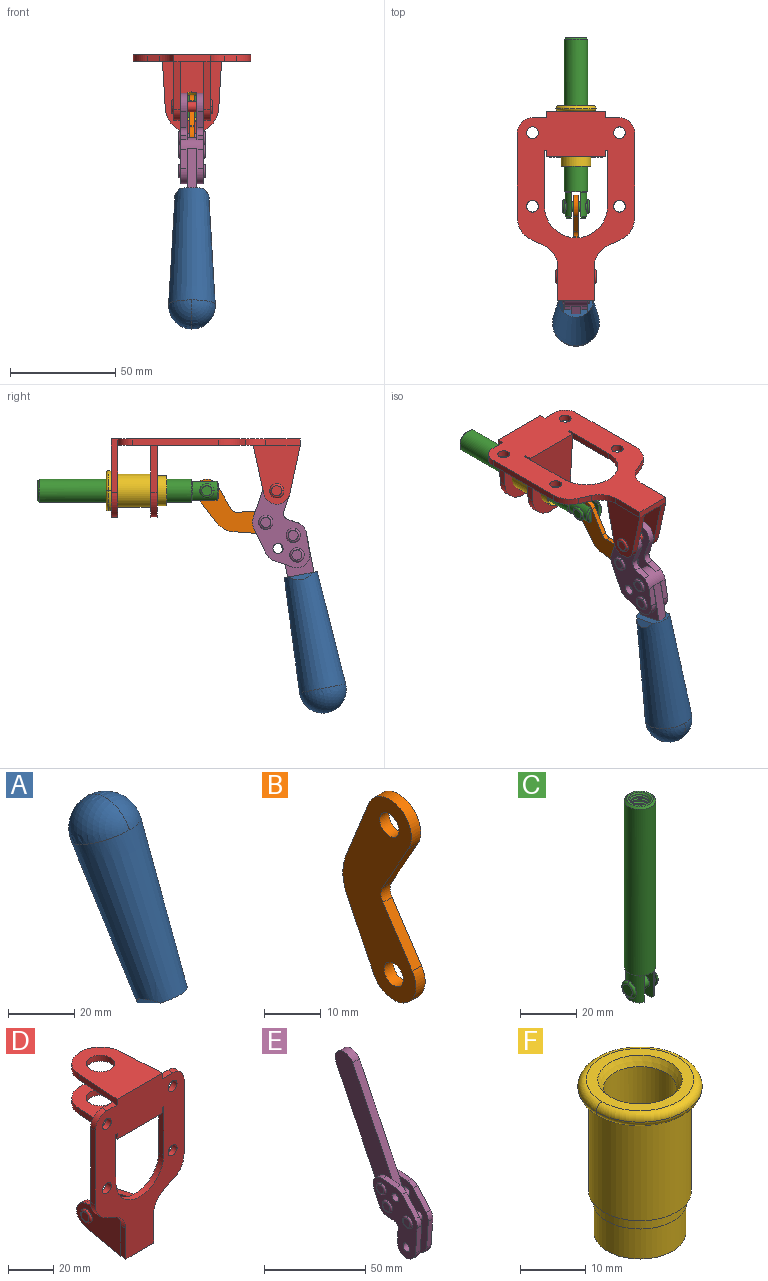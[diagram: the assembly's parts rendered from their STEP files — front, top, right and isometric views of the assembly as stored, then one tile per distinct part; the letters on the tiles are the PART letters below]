
ASSEMBLY  parts=6 mates=6
PART A: 11 faces, bbox 22.3x42.6x64.5 mm
  f0: sphere r=11.13mm, area 411.4mm2, adj f1,f8
  f1: cone r=11.11mm half-angle=3.3deg, axis (0,0.44,0.9), area 3251.8mm2, adj f0,f7,f8,f9,f10
  f2: cylinder r=6.16mm len=11.7mm, axis (1,0,0), area 89.5mm2, adj f3,f4,f5,f6
  f3: plane 60.23x36.75mm, normal (-1,0,0), area 763.6mm2, adj f2,f4,f6,f10
  f4: plane 51.37x25.05mm, normal (0,0.9,-0.44), area 264.2mm2, adj f2,f3,f5,f10
  f5: plane 60.23x36.75mm, normal (1,0,0), area 763.6mm2, adj f2,f4,f6,f10
  f6: plane 51.37x25.05mm, normal (0,-0.9,0.44), area 264.2mm2, adj f2,f3,f5,f10
  f7: plane 9.95x5.95mm, normal (0.71,-0.31,-0.64), area 25.8mm2, adj f1,f10
  f8: sphere r=11.13mm, area 411.4mm2, adj f0,f1
  f9: plane 9.95x5.95mm, normal (-0.71,-0.31,-0.64), area 25.8mm2, adj f1,f10
  f10: plane 14.27x11.38mm, normal (0,-0.44,-0.9), area 106.7mm2, adj f1,f3,f4,f5,f6,f7,f9
PART B: 12 faces, bbox 2.3x18.2x42.8 mm
  f0: cylinder r=2.4mm len=4.8mm, axis (1,0,0), area 34.9mm2, adj f4,f11
  f1: cylinder r=10.41mm len=8.47mm, axis (1,0,0), area 20.2mm2, adj f4,f9,f10,f11
  f2: cylinder r=3.05mm len=3.16mm, axis (1,0,0), area 7.7mm2, adj f4,f6,f7,f11
  f3: cylinder r=2.4mm len=4.8mm, axis (1,0,0), area 34.9mm2, adj f4,f11
  f4: plane 42.81x18.23mm, normal (-1,0,0), area 414.1mm2, adj f0,f1,f2,f3,f5,f6,f7,f8
  f5: cylinder r=5.54mm len=10.67mm, axis (1,0,0), area 41.8mm2, adj f4,f6,f10,f11
  f6: plane 11.66x6.53mm, normal (0,-0.87,-0.49), area 30.9mm2, adj f2,f4,f5,f11
  f7: plane 11.17x7.33mm, normal (0,-0.84,0.55), area 30.9mm2, adj f2,f4,f8,f11
  f8: cylinder r=5.54mm len=10.51mm, axis (1,0,0), area 41.8mm2, adj f4,f7,f9,f11
  f9: plane 13.67x6.67mm, normal (0,0.9,-0.44), area 35.1mm2, adj f1,f4,f8,f11
  f10: plane 14.1x5.7mm, normal (0,0.93,0.37), area 35.1mm2, adj f1,f4,f5,f11
  f11: plane 42.81x18.23mm, normal (1,0,0), area 414.1mm2, adj f0,f1,f2,f3,f5,f6,f7,f8
PART C: 48 faces, bbox 12.6x11.1x86.1 mm
  f0: torus R=2.41mm, axis (-1,0,0), area 15mm2, adj f30,f32,f34
  f1: torus R=2.41mm, axis (-1,0,0), area 15mm2, adj f29,f31,f33
  f2: cylinder r=5.54mm len=72.39mm, axis (0,0,1), area 2518.5mm2, adj f3,f4,f42,f43
  f3: cone r=5.54mm half-angle=45deg, axis (0,0,1), area 7.6mm2, adj f2,f5,f41
  f4: cone r=5.54mm half-angle=45deg, axis (0,0,-1), area 34.9mm2, adj f2,f39
  f5: cylinder r=5.08mm len=11.48mm, axis (0,0,1), area 108.3mm2, adj f3,f7,f8,f41
  f6: cylinder r=2.41mm len=4.83mm, axis (-1,0,0), area 71.2mm2, adj f40,f41
  f7: cylinder r=2.41mm len=4.83mm, axis (-1,0,0), area 7.6mm2, adj f5,f34
  f8: cone r=5.08mm half-angle=45deg, axis (0,0,1), area 10.6mm2, adj f5,f37,f41
  f9: cone r=3.98mm half-angle=45deg, axis (0,0,1), area 17.6mm2, adj f27,f39,f45,f46,f47
  f10: cylinder r=2.41mm len=4.83mm, axis (-1,0,0), area 7.6mm2, adj f33,f38
  f11: cylinder r=3.2mm len=6.4mm, axis (0,0,1), area 78.4mm2, adj f12,f28,f44,f45,f47
  f12: cylinder r=3.2mm len=6.4mm, axis (0,0,1), area 10.5mm2, adj f11,f13,f45,f47
  f13: cylinder r=3.2mm len=6.4mm, axis (0,0,1), area 10.5mm2, adj f12,f14,f45,f47
  f14: cylinder r=3.2mm len=6.4mm, axis (0,0,1), area 10.5mm2, adj f13,f15,f45,f47
  f15: cylinder r=3.2mm len=6.4mm, axis (0,0,1), area 10.5mm2, adj f14,f16,f45,f47
  f16: cylinder r=3.2mm len=6.4mm, axis (0,0,1), area 10.5mm2, adj f15,f17,f45,f47
  f17: cylinder r=3.2mm len=6.4mm, axis (0,0,1), area 10.5mm2, adj f16,f18,f45,f47
  f18: cylinder r=3.2mm len=6.4mm, axis (0,0,1), area 10.5mm2, adj f17,f19,f45,f47
  f19: cylinder r=3.2mm len=6.4mm, axis (0,0,1), area 10.5mm2, adj f18,f20,f45,f47
  f20: cylinder r=3.2mm len=6.4mm, axis (0,0,1), area 10.5mm2, adj f19,f21,f45,f47
  f21: cylinder r=3.2mm len=6.4mm, axis (0,0,1), area 10.5mm2, adj f20,f22,f45,f47
  f22: cylinder r=3.2mm len=6.4mm, axis (0,0,1), area 10.5mm2, adj f21,f23,f45,f47
  f23: cylinder r=3.2mm len=6.4mm, axis (0,0,1), area 10.5mm2, adj f22,f24,f45,f47
  f24: cylinder r=3.2mm len=6.4mm, axis (0,0,1), area 10.5mm2, adj f23,f25,f45,f47
  f25: cylinder r=3.2mm len=6.4mm, axis (0,0,1), area 10.5mm2, adj f24,f26,f45,f47
  f26: cylinder r=3.2mm len=6.4mm, axis (0,0,1), area 10.5mm2, adj f25,f27,f45,f47
  f27: cylinder r=3.2mm len=6.4mm, axis (0,0,1), area 7.4mm2, adj f9,f26,f45,f47
  f28: cone r=3.2mm half-angle=60deg, axis (0,0,1), area 37.2mm2, adj f11
  f29: plane 4.83x4.83mm, normal (-1,0,0), area 18.3mm2, adj f1,f31
  f30: plane 4.83x4.83mm, normal (1,0,0), area 18.3mm2, adj f0,f32
  f31: torus R=2.41mm, axis (-1,0,0), area 15mm2, adj f1,f29,f33
  f32: torus R=2.41mm, axis (-1,0,0), area 15mm2, adj f0,f30,f34
  f33: plane 6.83x6.83mm, normal (1,0,0), area 18.3mm2, adj f1,f10,f31
  f34: plane 6.83x6.83mm, normal (-1,0,0), area 18.3mm2, adj f0,f7,f32
  f35: cone r=5.08mm half-angle=45deg, axis (0,0,1), area 10.6mm2, adj f36,f38,f40
  f36: plane 7.25x1.97mm, normal (0,0,-1), area 10mm2, adj f35,f40
  f37: plane 7.25x1.97mm, normal (0,0,-1), area 10mm2, adj f8,f41
  f38: cylinder r=5.08mm len=11.48mm, axis (0,0,1), area 108.3mm2, adj f10,f35,f40,f42
  f39: plane 9.55x9.55mm, normal (0,0,1), area 22mm2, adj f4,f9
  f40: plane 12.76x10.09mm, normal (1,0,0), area 95.7mm2, adj f6,f35,f36,f38,f42,f43
  f41: plane 12.76x10.09mm, normal (-1,0,0), area 95.7mm2, adj f3,f5,f6,f8,f37,f43
  f42: cone r=5.54mm half-angle=45deg, axis (0,0,1), area 7.6mm2, adj f2,f38,f40
  f43: plane 11.07x4.7mm, normal (0,0,-1), area 50.4mm2, adj f2,f40,f41
  f44: plane 0.89x0.62mm, normal (-1,0,0), area 0.3mm2, adj f11,f45,f46,f47
  f45: bspline ~24.8x7.63mm, area 266.6mm2, adj f9,f11,f12,f13,f14,f15,f16,f17
  f46: bspline ~24.87x7.63mm, area 73.6mm2, adj f9,f44,f45,f47
  f47: bspline ~24.98x7.63mm, area 272.5mm2, adj f9,f11,f12,f13,f14,f15,f16,f17
PART D: 55 faces, bbox 55.7x37.4x89.8 mm
  f0: torus R=2.41mm, axis (-1,0,0), area 15mm2, adj f11,f15,f25
  f1: torus R=2.41mm, axis (-1,0,0), area 15mm2, adj f10,f12,f22
  f2: cylinder r=2.78mm len=5.56mm, axis (0,-1,0), area 54.2mm2, adj f30,f54
  f3: cylinder r=14.99mm len=29.97mm, axis (0,-1,0), area 145.9mm2, adj f30,f49,f53,f54
  f4: cylinder r=2.78mm len=5.56mm, axis (0,-1,0), area 54.2mm2, adj f30,f54
  f5: cylinder r=2.78mm len=5.56mm, axis (0,-1,0), area 54.2mm2, adj f30,f54
  f6: cylinder r=2.78mm len=5.56mm, axis (0,-1,0), area 54.2mm2, adj f30,f54
  f7: cylinder r=6.35mm len=12.7mm, axis (0,0,1), area 123.6mm2, adj f27,f51
  f8: cylinder r=6.35mm len=12.7mm, axis (0,0,-1), area 124.7mm2, adj f21,f35
  f9: cylinder r=2.41mm len=11.18mm, axis (-1,0,0), area 169.4mm2, adj f16,f19
  f10: plane 4.83x4.83mm, normal (1,0,0), area 18.3mm2, adj f1,f12
  f11: plane 4.83x4.83mm, normal (-1,0,0), area 18.3mm2, adj f0,f15
  f12: torus R=2.41mm, axis (-1,0,0), area 15mm2, adj f1,f10,f22
  f13: cylinder r=6.35mm len=12.41mm, axis (1,0,0), area 53.4mm2, adj f18,f19,f22,f23
  f14: cylinder r=6.35mm len=12.41mm, axis (-1,0,0), area 53.4mm2, adj f16,f17,f24,f25
  f15: torus R=2.41mm, axis (-1,0,0), area 15mm2, adj f0,f11,f25
  f16: plane 27.86x22.35mm, normal (1,0,0), area 425.4mm2, adj f9,f14,f17,f24,f30
  f17: plane 22.86x4.97mm, normal (0,0.21,0.98), area 72.5mm2, adj f14,f16,f25,f30
  f18: plane 22.86x4.97mm, normal (0,0.21,0.98), area 72.5mm2, adj f13,f19,f22,f30
  f19: plane 27.86x22.35mm, normal (-1,0,0), area 425.4mm2, adj f9,f13,f18,f23,f30
  f20: cylinder r=12.7mm len=25.35mm, axis (0,0,-1), area 119.8mm2, adj f21,f34,f35,f36
  f21: plane 34.21x28.07mm, normal (0,0,-1), area 702.4mm2, adj f8,f20,f30,f34,f36
  f22: plane 27.96x22.45mm, normal (1,0,0), area 407.2mm2, adj f1,f12,f13,f18,f23,f30,f42,f43
  f23: plane 22.86x4.97mm, normal (0,0.21,-0.98), area 72.5mm2, adj f13,f19,f22,f44
  f24: plane 22.86x4.97mm, normal (0,0.21,-0.98), area 72.5mm2, adj f14,f16,f25,f44
  f25: plane 27.86x22.35mm, normal (-1,0,0), area 407.1mm2, adj f0,f14,f15,f17,f24,f30,f45,f46
  f26: plane 3.1x0.95mm, normal (0,0,-1), area 2.7mm2, adj f30,f49,f50,f54
  f27: plane 34.21x28.07mm, normal (0,0,1), area 702.4mm2, adj f7,f28,f30,f50,f52
  f28: cylinder r=12.7mm len=25.35mm, axis (0,0,1), area 118.8mm2, adj f27,f50,f51,f52
  f29: plane 3.1x0.95mm, normal (0,0,-1), area 2.7mm2, adj f30,f52,f53,f54
  f30: plane 86.54x55.63mm, normal (0,1,0), area 2362.9mm2, adj f2,f3,f4,f5,f6,f16,f17,f18
  f31: plane 40.56x3.1mm, normal (-1,0,0), area 125.7mm2, adj f30,f32,f48,f54
  f32: cylinder r=7.11mm len=7.11mm, axis (0,-1,0), area 34.6mm2, adj f30,f31,f33,f54
  f33: plane 6.67x3.1mm, normal (0,0,1), area 20.4mm2, adj f30,f32,f34,f54
  f34: plane 25.39x3.13mm, normal (-1,0.06,0), area 79.5mm2, adj f20,f21,f33,f35,f54
  f35: plane 37.31x28.45mm, normal (0,0,1), area 789.9mm2, adj f8,f20,f34,f36,f54
  f36: plane 25.39x3.13mm, normal (1,0.06,0), area 79.5mm2, adj f20,f21,f35,f37,f54
  f37: plane 6.67x3.1mm, normal (0,0,1), area 20.4mm2, adj f30,f36,f38,f54
  f38: cylinder r=7.11mm len=7.11mm, axis (0,-1,0), area 34.6mm2, adj f30,f37,f39,f54
  f39: plane 40.56x3.1mm, normal (1,0,0), area 125.7mm2, adj f30,f38,f40,f54
  f40: cylinder r=11.18mm len=10.16mm, axis (0,-1,0), area 39.5mm2, adj f30,f39,f41,f54
  f41: plane 6.09x3.1mm, normal (0.42,0,-0.91), area 20.8mm2, adj f30,f40,f42,f54
  f42: cylinder r=11.18mm len=9.41mm, axis (0,-1,0), area 37.2mm2, adj f22,f30,f41,f43,f54
  f43: plane 16.5x3.1mm, normal (1,0,0), area 51.1mm2, adj f22,f42,f44,f54
  f44: plane 17.37x3.1mm, normal (0,0,-1), area 53.8mm2, adj f23,f24,f30,f43,f45,f54
  f45: plane 16.5x3.1mm, normal (-1,0,0), area 51.1mm2, adj f25,f44,f46,f54
  f46: cylinder r=11.18mm len=9.41mm, axis (0,-1,0), area 37.2mm2, adj f25,f30,f45,f47,f54
  f47: plane 6.09x3.1mm, normal (-0.42,0,-0.91), area 20.8mm2, adj f30,f46,f48,f54
  f48: cylinder r=11.18mm len=10.16mm, axis (0,-1,0), area 39.5mm2, adj f30,f31,f47,f54
  f49: plane 26.54x3.1mm, normal (-1,0,0), area 82.3mm2, adj f3,f26,f30,f54
  f50: plane 25.39x3.1mm, normal (1,0.06,0), area 78.8mm2, adj f26,f27,f28,f51,f54
  f51: plane 37.31x28.45mm, normal (0,0,-1), area 789.9mm2, adj f7,f28,f50,f52,f54
  f52: plane 25.39x3.1mm, normal (-1,0.06,0), area 78.8mm2, adj f27,f28,f29,f51,f54
  f53: plane 26.54x3.1mm, normal (1,0,0), area 82.3mm2, adj f3,f29,f30,f54
  f54: plane 89.66x55.63mm, normal (0,-1,0), area 2678.5mm2, adj f2,f3,f4,f5,f6,f26,f29,f31
PART E: 59 faces, bbox 12.9x60.2x99.6 mm
  f0: torus R=2.39mm, axis (-1,0,0), area 14.9mm2, adj f20,f43,f51
  f1: torus R=2.39mm, axis (-1,0,0), area 14.9mm2, adj f19,f42,f51
  f2: torus R=2.39mm, axis (-1,0,0), area 14.9mm2, adj f18,f35,f51
  f3: torus R=2.39mm, axis (-1,0,0), area 14.9mm2, adj f14,f17,f23
  f4: torus R=2.39mm, axis (-1,0,0), area 14.9mm2, adj f13,f16,f23
  f5: torus R=2.39mm, axis (-1,0,0), area 14.9mm2, adj f12,f15,f23
  f6: cylinder r=2.39mm len=4.78mm, axis (1,0,0), area 46.5mm2, adj f48,f50,f51
  f7: cylinder r=2.39mm len=4.78mm, axis (1,0,0), area 46.5mm2, adj f50,f51
  f8: cylinder r=6.35mm len=12.68mm, axis (1,0,0), area 61.8mm2, adj f38,f39,f50,f51
  f9: cylinder r=2.39mm len=4.78mm, axis (-1,0,0), area 70.5mm2, adj f46,f50
  f10: cylinder r=2.39mm len=4.78mm, axis (-1,0,0), area 46.5mm2, adj f23,f45,f46
  f11: cylinder r=2.39mm len=4.78mm, axis (-1,0,0), area 46.5mm2, adj f23,f46
  f12: plane 4.78x4.78mm, normal (1,0,0), area 17.9mm2, adj f5,f15
  f13: plane 4.78x4.78mm, normal (1,0,0), area 17.9mm2, adj f4,f16
  f14: plane 4.78x4.78mm, normal (1,0,0), area 17.9mm2, adj f3,f17
  f15: torus R=2.39mm, axis (-1,0,0), area 14.9mm2, adj f5,f12,f23
  f16: torus R=2.39mm, axis (-1,0,0), area 14.9mm2, adj f4,f13,f23
  f17: torus R=2.39mm, axis (-1,0,0), area 14.9mm2, adj f3,f14,f23
  f18: plane 4.78x4.78mm, normal (-1,0,0), area 17.9mm2, adj f2,f35
  f19: plane 4.78x4.78mm, normal (-1,0,0), area 17.9mm2, adj f1,f42
  f20: plane 4.78x4.78mm, normal (-1,0,0), area 17.9mm2, adj f0,f43
  f21: plane 2.26x0.2mm, normal (1,0,0), area 0.2mm2, adj f31,f44
  f22: plane 2.26x0.2mm, normal (-1,0,0), area 0.2mm2, adj f41,f44
  f23: plane 39.37x30.77mm, normal (1,0,0), area 565.5mm2, adj f3,f4,f5,f10,f11,f15,f16,f17
  f24: cylinder r=6.1mm len=4.15mm, axis (-1,0,0), area 14.7mm2, adj f23,f25,f32,f46
  f25: plane 10.25x9.01mm, normal (0,-0.75,0.66), area 42.3mm2, adj f23,f24,f26,f46
  f26: cylinder r=6.35mm len=4.64mm, axis (-1,0,0), area 15.6mm2, adj f23,f25,f27,f46
  f27: plane 15.84x3.1mm, normal (0,-1,-0.07), area 49.2mm2, adj f23,f26,f28,f46
  f28: cylinder r=6.35mm len=12.68mm, axis (-1,0,0), area 61.8mm2, adj f23,f27,f29,f46
  f29: plane 8.11x3.1mm, normal (0,1,0.07), area 25.2mm2, adj f23,f28,f30,f46
  f30: cylinder r=3.05mm len=3.25mm, axis (-1,0,0), area 14.8mm2, adj f23,f29,f31,f46
  f31: plane 5.99x3.1mm, normal (0,0.07,-1), area 18.6mm2, adj f21,f23,f30,f44,f46
  f32: plane 9.5x3.1mm, normal (0,-0.07,1), area 29.5mm2, adj f23,f24,f33,f46,f47
  f33: cylinder r=6.1mm len=8.63mm, axis (-1,0,0), area 39.1mm2, adj f23,f32,f34,f47
  f34: plane 8.65x3.96mm, normal (0,0.91,-0.42), area 29.5mm2, adj f23,f33,f44,f47
  f35: torus R=2.39mm, axis (-1,0,0), area 14.9mm2, adj f2,f18,f51
  f36: plane 10.25x9.01mm, normal (0,-0.75,0.66), area 42.3mm2, adj f37,f49,f50,f51
  f37: cylinder r=6.35mm len=4.64mm, axis (1,0,0), area 15.6mm2, adj f36,f38,f50,f51
  f38: plane 15.84x3.1mm, normal (0,-1,-0.07), area 49.2mm2, adj f8,f37,f50,f51
  f39: plane 8.11x3.1mm, normal (0,1,0.07), area 25.2mm2, adj f8,f40,f50,f51
  f40: cylinder r=3.05mm len=3.25mm, axis (1,0,0), area 14.8mm2, adj f39,f41,f50,f51
  f41: plane 5.99x3.1mm, normal (0,0.07,-1), area 18.6mm2, adj f22,f40,f44,f50,f51
  f42: torus R=2.39mm, axis (-1,0,0), area 14.9mm2, adj f1,f19,f51
  f43: torus R=2.39mm, axis (-1,0,0), area 14.9mm2, adj f0,f20,f51
  f44: cylinder r=6.35mm len=12.12mm, axis (-1,0,0), area 128.9mm2, adj f21,f22,f23,f31,f34,f41,f46,f47
  f45: plane 2.65x1.35mm, normal (1,0,0), area 1mm2, adj f10,f55
  f46: plane 39.08x20.42mm, normal (-1,0,0), area 412.5mm2, adj f9,f10,f11,f24,f25,f26,f27,f28
  f47: plane 77.62x39.82mm, normal (1,0,0), area 850mm2, adj f32,f33,f34,f44,f53,f54,f55
  f48: plane 2.65x1.35mm, normal (-1,0,0), area 1mm2, adj f6,f55
  f49: cylinder r=6.1mm len=4.15mm, axis (1,0,0), area 14.7mm2, adj f36,f50,f51,f56
  f50: plane 39.08x20.42mm, normal (1,0,0), area 412.5mm2, adj f6,f7,f8,f9,f36,f37,f38,f39
  f51: plane 39.37x30.77mm, normal (-1,0,0), area 565.5mm2, adj f0,f1,f2,f6,f7,f8,f35,f36
  f52: plane 8.65x3.96mm, normal (0,0.91,-0.42), area 29.5mm2, adj f44,f51,f57,f58
  f53: plane 68.49x33.4mm, normal (0,0.9,-0.44), area 358.1mm2, adj f44,f47,f54,f58
  f54: cylinder r=6.35mm len=12.06mm, axis (1,0,0), area 93.7mm2, adj f47,f53,f55,f58
  f55: plane 68.49x33.4mm, normal (0,-0.9,0.44), area 358.1mm2, adj f44,f45,f46,f47,f48,f50,f54,f58
  f56: plane 9.5x3.1mm, normal (0,-0.07,1), area 29.5mm2, adj f49,f50,f51,f57,f58
  f57: cylinder r=6.1mm len=8.63mm, axis (1,0,0), area 39.1mm2, adj f51,f52,f56,f58
  f58: plane 77.62x39.82mm, normal (-1,0,0), area 850mm2, adj f44,f52,f53,f54,f55,f56,f57
PART F: 15 faces, bbox 20.6x20.6x28.7 mm
  f0: torus R=8.26mm, axis (0,0,1), area 56.8mm2, adj f1,f10,f12
  f1: torus R=8.26mm, axis (0,0,1), area 56.8mm2, adj f0,f6,f13
  f2: cylinder r=5.59mm len=25.91mm, axis (0,0,1), area 909.6mm2, adj f3,f4
  f3: cone r=6.86mm half-angle=45deg, axis (0,0,-1), area 70.2mm2, adj f2,f14
  f4: cone r=6.47mm half-angle=30deg, axis (0,0,1), area 66.7mm2, adj f2,f13
  f5: cylinder r=7.04mm len=14.07mm, axis (0,0,1), area 252.6mm2, adj f11,f14
  f6: torus R=8.26mm, axis (0,0,1), area 56.8mm2, adj f1,f12,f13
  f7: cylinder r=7.16mm len=14.33mm, axis (0,0,1), area 91.5mm2, adj f9,f11
  f8: cylinder r=7.86mm len=18.42mm, axis (0,0,1), area 909.6mm2, adj f9,f10
  f9: plane 15.72x15.72mm, normal (0,0,-1), area 33mm2, adj f7,f8
  f10: plane 16.51x16.51mm, normal (0,0,-1), area 19.9mm2, adj f0,f8,f12
  f11: plane 14.33x14.33mm, normal (0,0,-1), area 5.7mm2, adj f5,f7
  f12: torus R=8.26mm, axis (0,0,1), area 56.8mm2, adj f0,f6,f10
  f13: plane 16.51x16.51mm, normal (0,0,1), area 82.7mm2, adj f1,f4,f6
  f14: plane 14.07x14.07mm, normal (0,0,-1), area 7.8mm2, adj f3,f5
PLACE A rot(axis=(-1,0,0),164.9deg) t=(-0.04,-9.1,-49.18)mm
PLACE B rot(axis=(-1,0,0),59.8deg) t=(0,-33.8,-11.12)mm
PLACE C rot(axis=(-1,0,0),90deg) t=(0,-23.52,0)mm
PLACE D rot(axis=(-1,0,0),90deg) t=(0,-9.14,0)mm fixed
PLACE E rot(axis=(-1,0,0),164.9deg) t=(0,-9.1,-49.18)mm
PLACE F rot(axis=(-1,0,0),90deg) t=(0,-9.14,0)mm
MATE fastened F.f2 <-> D.f7  axis (0,-1,0) through (0,37.25,-24.61)mm
MATE fastened A.f2 <-> E.f54  axis (1,0,0) through (-2.35,-63.4,-120.58)mm
MATE revolute E.f7 <-> D.f0  axis (-1,0,0) through (0,-41.23,-24.61)mm
MATE slider C.f2 <-> F.f2  axis (0,1,0) through (0,35.26,-24.61)mm
MATE revolute B.f5 <-> C.f6  axis (1,0,0) through (0,-8.05,-24.61)mm
MATE revolute B.f3 <-> E.f4  axis (1,0,0) through (0,-36.03,-39.61)mm
